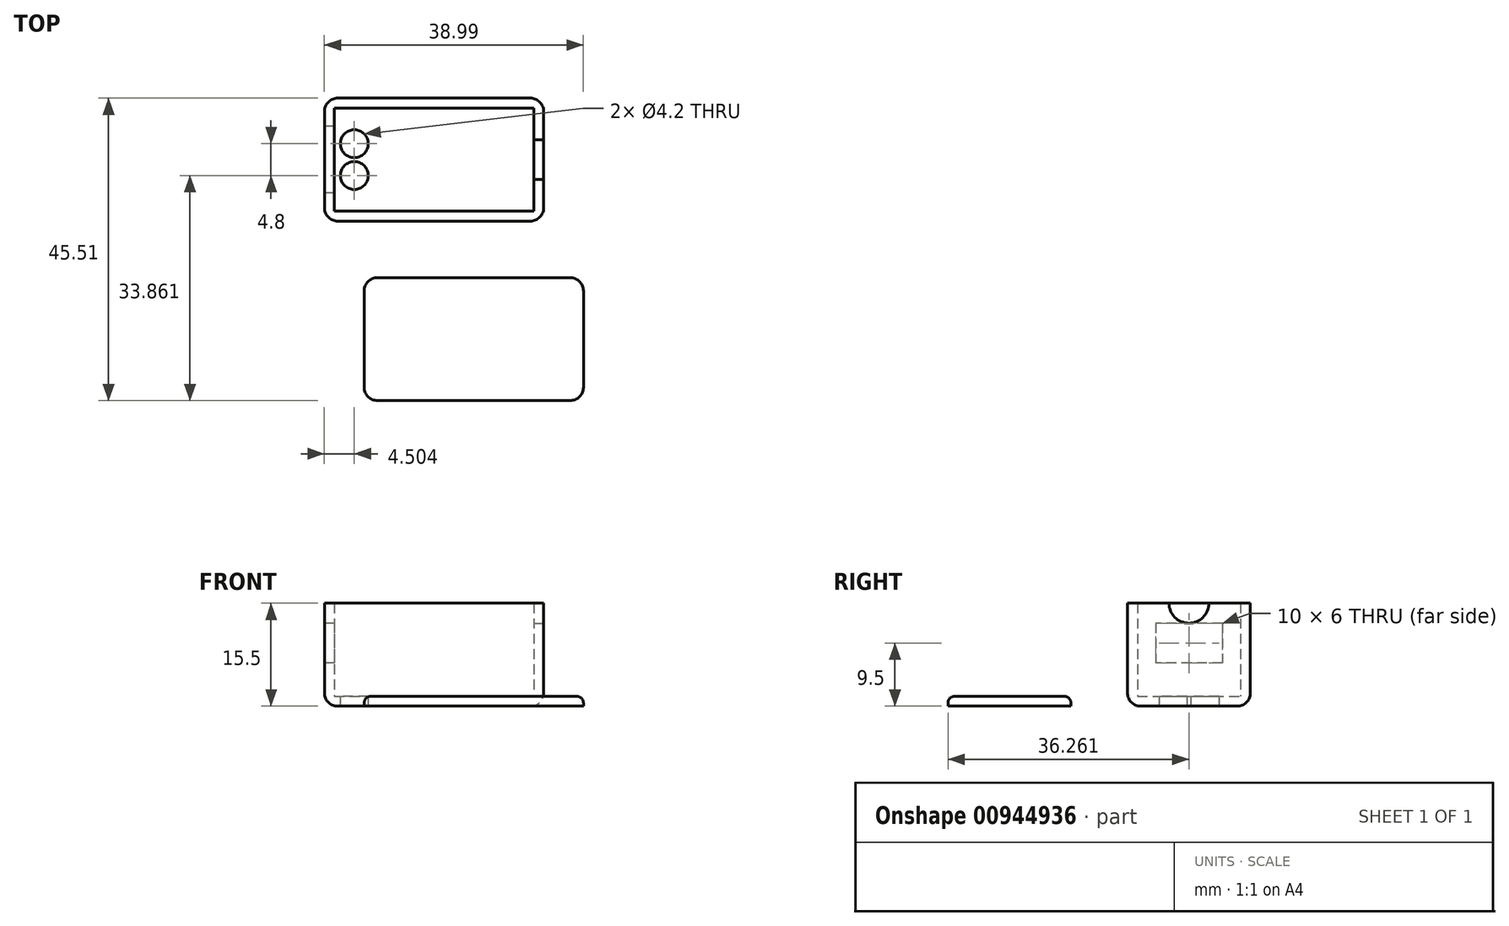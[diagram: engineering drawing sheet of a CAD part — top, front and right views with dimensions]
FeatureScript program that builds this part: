
annotation { "Feature Type Name" : "Feature", "Feature Type Description" : "" }
export const myFeature = defineFeature(function(context is Context, id is Id, definition is map)
    precondition{}
    {
        {
            var Q0;
            Q0=qCreatedBy(makeId("Top.planeOp"),FACE);
            var sketch = newSketch(context, id + "F0", { "sketchPlane" : qUnion([Q0])});
            skLineSegment(sketch, "E0.bottom", {"start": v(-24.86, -16.36) * mm, "end": v(5.14, -16.36) * mm});
            skLineSegment(sketch, "E0.top", {"start": v(-24.86, -0.86) * mm, "end": v(5.14, -0.86) * mm});
            skLineSegment(sketch, "E0.left", {"start": v(-24.86, -16.36) * mm, "end": v(-24.86, -0.86) * mm});
            skLineSegment(sketch, "E0.right", {"start": v(5.14, -16.36) * mm, "end": v(5.14, -0.86) * mm});
            skLineSegment(sketch, "E1.0", {"start": v(-26.36, -15.86) * mm, "end": v(-26.36, -1.36) * mm});
            skLineSegment(sketch, "E1.1", {"start": v(-24.36, -17.86) * mm, "end": v(4.64, -17.86) * mm});
            skLineSegment(sketch, "E1.2", {"start": v(6.64, -15.86) * mm, "end": v(6.64, -1.36) * mm});
            skLineSegment(sketch, "E1.3", {"start": v(-24.36, 0.64) * mm, "end": v(4.64, 0.64) * mm});
            skPoint(sketch, "E2.visualSharp", {"position": v(6.64, 0.64) * mm});
            skArc(sketch, "E2.filletArc", {"start": v(6.64, -1.36) * mm, "mid": v(6.06, 0.06) * mm, "end": v(4.64, 0.64) * mm});
            skPoint(sketch, "E3.visualSharp", {"position": v(6.64, -17.86) * mm});
            skArc(sketch, "E3.filletArc", {"start": v(4.64, -17.86) * mm, "mid": v(6.06, -17.27) * mm, "end": v(6.64, -15.86) * mm});
            skPoint(sketch, "E4.visualSharp", {"position": v(-26.36, -17.86) * mm});
            skArc(sketch, "E4.filletArc", {"start": v(-26.36, -15.86) * mm, "mid": v(-25.77, -17.27) * mm, "end": v(-24.36, -17.86) * mm});
            skPoint(sketch, "E5.visualSharp", {"position": v(-26.36, 0.64) * mm});
            skArc(sketch, "E5.filletArc", {"start": v(-24.36, 0.64) * mm, "mid": v(-25.77, 0.06) * mm, "end": v(-26.36, -1.36) * mm});
            skLineSegment(sketch, "E6", {"start": v(-24.86, -8.6) * mm, "end": v(-21.86, -8.6) * mm, "construction": true});
            skLineSegment(sketch, "E7", {"start": v(-21.86, -8.6) * mm, "end": v(-21.86, -6.2) * mm, "construction": true});
            skLineSegment(sketch, "E8", {"start": v(-21.86, -8.6) * mm, "end": v(-21.86, -11) * mm, "construction": true});
            skCircle(sketch, "E9", {"center": v(-21.86, -6.2) * mm, "radius": 2.1 * mm});
            skCircle(sketch, "E10", {"center": v(-21.86, -11) * mm, "radius": 2.1 * mm});
            skSolve(sketch);
        }
        {
            var Q0;
            Q0=makeQuery(id+"F0.imprint","IMPRINT",FACE,{"disambiguationData":[TD([[makeQuery(id+"F0.imprint","IMPRINT",EDGE,{"derivedFrom":sQuery(id+"F0.wireOp",EDGE,"E0.bottom")}),-1.0]])]});
            extrude(context, id + "F1", {"entities" : qUnion([Q0]), "depth" : 15.5 * mm, "offsetDistance" : 25 * mm});
        }
        {
            var Q0;
            Q0=makeQuery(id+"F0.imprint","IMPRINT",FACE,{"disambiguationData":[TD([[makeQuery(id+"F0.imprint","IMPRINT",EDGE,{"derivedFrom":sQuery(id+"F0.wireOp",EDGE,"E0.bottom")}),1.0]])]});
            extrude(context, id + "F2", {"entities" : qUnion([Q0]), "operationType" : NewBodyOperationType.ADD, "depth" : 1.5 * mm, "offsetDistance" : 25 * mm});
        }
        {
            var Q0;
            Q0=makeQuery(id+"F1.opExtrude","SWEPT_FACE",FACE,{"disambiguationData":[OSD([sQuery(id+"F0.wireOp",EDGE,"E1.0")])]});
            var sketch = newSketch(context, id + "F3", { "sketchPlane" : qUnion([Q0])});
            skLineSegment(sketch, "E11", {"start": v(8.6, 15.5) * mm, "end": v(8.6, 12.5) * mm, "construction": true});
            skLineSegment(sketch, "E12", {"start": v(8.6, 12.5) * mm, "end": v(3.6, 12.5) * mm, "construction": true});
            skLineSegment(sketch, "E13.bottom", {"start": v(3.6, 12.5) * mm, "end": v(13.6, 12.5) * mm});
            skLineSegment(sketch, "E13.top", {"start": v(3.6, 6.5) * mm, "end": v(13.6, 6.5) * mm});
            skLineSegment(sketch, "E13.left", {"start": v(3.6, 12.5) * mm, "end": v(3.6, 6.5) * mm});
            skLineSegment(sketch, "E13.right", {"start": v(13.6, 12.5) * mm, "end": v(13.6, 6.5) * mm});
            skSolve(sketch);
        }
        {
            var Q0;
            Q0=makeQuery(id+"F3.imprint","IMPRINT",FACE,{"disambiguationData":[TD([[makeQuery(id+"F3.imprint","IMPRINT",EDGE,{"derivedFrom":sQuery(id+"F3.wireOp",EDGE,"E13.bottom")}),-1.0]])]});
            extrude(context, id + "F4", {"entities" : qUnion([Q0]), "operationType" : NewBodyOperationType.REMOVE, "oppositeDirection" : true, "depth" : 2 * mm, "offsetDistance" : 25 * mm});
        }
        {
            var Q0;
            Q0=qCreatedBy(makeId("Top.planeOp"),FACE);
            var sketch = newSketch(context, id + "F5", { "sketchPlane" : qUnion([Q0])});
            skLineSegment(sketch, "E14.bottom", {"start": v(-18.37, -26.37) * mm, "end": v(10.63, -26.37) * mm});
            skLineSegment(sketch, "E14.top", {"start": v(-18.37, -44.87) * mm, "end": v(10.63, -44.87) * mm});
            skLineSegment(sketch, "E14.left", {"start": v(-20.37, -28.37) * mm, "end": v(-20.37, -42.87) * mm});
            skLineSegment(sketch, "E14.right", {"start": v(12.63, -28.37) * mm, "end": v(12.63, -42.87) * mm});
            skPoint(sketch, "E15.visualSharp", {"position": v(12.63, -26.37) * mm});
            skArc(sketch, "E15.filletArc", {"start": v(12.63, -28.37) * mm, "mid": v(12.05, -26.96) * mm, "end": v(10.63, -26.37) * mm});
            skPoint(sketch, "E16.visualSharp", {"position": v(12.63, -44.87) * mm});
            skArc(sketch, "E16.filletArc", {"start": v(10.63, -44.87) * mm, "mid": v(12.05, -44.29) * mm, "end": v(12.63, -42.87) * mm});
            skPoint(sketch, "E17.visualSharp", {"position": v(-20.37, -44.87) * mm});
            skArc(sketch, "E17.filletArc", {"start": v(-20.37, -42.87) * mm, "mid": v(-19.78, -44.29) * mm, "end": v(-18.37, -44.87) * mm});
            skPoint(sketch, "E18.visualSharp", {"position": v(-20.37, -26.37) * mm});
            skArc(sketch, "E18.filletArc", {"start": v(-18.37, -26.37) * mm, "mid": v(-19.78, -26.96) * mm, "end": v(-20.37, -28.37) * mm});
            skSolve(sketch);
        }
        {
            var Q0;
            Q0=makeQuery(id+"F5.imprint","IMPRINT",FACE,{"disambiguationData":[TD([[makeQuery(id+"F5.imprint","IMPRINT",EDGE,{"derivedFrom":sQuery(id+"F5.wireOp",EDGE,"E14.bottom")}),-1.0]])]});
            extrude(context, id + "F6", {"entities" : qUnion([Q0]), "depth" : 1.5 * mm, "offsetDistance" : 25 * mm});
        }
        {
            var Q0;
            Q0=makeQuery(id+"F6.opExtrude","CAP_EDGE",EDGE,{"disambiguationData":[OSD([sQuery(id+"F5.wireOp",EDGE,"E14.top")])],"isStart":false});
            fillet(context, id + "F7", {"entities" : qUnion([Q0]), "radius" : 1 * mm, "tangentPropagation" : true, "allowEdgeOverflow" : false});
        }
        {
            var Q0;
            Q0=makeQuery(id+"F1.opExtrude","CAP_EDGE",EDGE,{"disambiguationData":[OSD([sQuery(id+"F0.wireOp",EDGE,"E1.0")])],"isStart":true});
            var Q1;
            Q1=makeQuery(id+"F1.opExtrude","CAP_EDGE",EDGE,{"disambiguationData":[OSD([sQuery(id+"F0.wireOp",EDGE,"E1.3")])],"isStart":true});
            var Q2;
            Q2=makeQuery(id+"F1.opExtrude","CAP_EDGE",EDGE,{"disambiguationData":[OSD([sQuery(id+"F0.wireOp",EDGE,"E1.2")])],"isStart":true});
            var Q3;
            Q3=makeQuery(id+"F1.opExtrude","CAP_EDGE",EDGE,{"disambiguationData":[OSD([sQuery(id+"F0.wireOp",EDGE,"E1.1")])],"isStart":true});
            var Q4;
            Q4=makeQuery(id+"F1.opExtrude","CAP_EDGE",EDGE,{"disambiguationData":[OSD([sQuery(id+"F0.wireOp",EDGE,"E3.filletArc")])],"isStart":true});
            var Q5;
            Q5=makeQuery(id+"F1.opExtrude","CAP_EDGE",EDGE,{"disambiguationData":[OSD([sQuery(id+"F0.wireOp",EDGE,"E2.filletArc")])],"isStart":true});
            var Q6;
            Q6=makeQuery(id+"F1.opExtrude","CAP_EDGE",EDGE,{"disambiguationData":[OSD([sQuery(id+"F0.wireOp",EDGE,"E5.filletArc")])],"isStart":true});
            var Q7;
            Q7=makeQuery(id+"F1.opExtrude","CAP_EDGE",EDGE,{"disambiguationData":[OSD([sQuery(id+"F0.wireOp",EDGE,"E4.filletArc")])],"isStart":true});
            fillet(context, id + "F8", {"entities" : qUnion([Q0, Q1, Q2, Q3, Q4, Q5, Q6, Q7]), "radius" : 2 * mm, "allowEdgeOverflow" : false});
        }
        {
            var Q0;
            Q0=makeQuery(id+"F1.opExtrude","SWEPT_FACE",FACE,{"disambiguationData":[OSD([sQuery(id+"F0.wireOp",EDGE,"E1.2")])]});
            var sketch = newSketch(context, id + "F9", { "sketchPlane" : qUnion([Q0])});
            skCircle(sketch, "E19", {"center": v(-8.6, 15.5) * mm, "radius": 3 * mm});
            skSolve(sketch);
        }
        {
            var Q0;
            {var subQ0=sQuery(id+"F9.wireOp",EDGE,"E19");var subQ1=makeQuery(id+"F1.opExtrude","CAP_EDGE",EDGE,{"disambiguationData":[OSD([sQuery(id+"F0.wireOp",EDGE,"E1.2")])],"isStart":false});var subQ2=makeQuery(id+"F9.imprint","INTERSECT",VERTEX,{"disambiguationData":[OD(0.0)],"derivedFrom":[subQ1,subQ0]});Q0=makeQuery(id+"F9.imprint","IMPRINT",FACE,{"disambiguationData":[TD([[makeQuery(id+"F9.imprint","IMPRINT",EDGE,{"disambiguationData":[TD([[subQ2,-1.0]])],"derivedFrom":subQ0}),1.0]])]});}
            extrude(context, id + "F10", {"entities" : qUnion([Q0]), "operationType" : NewBodyOperationType.REMOVE, "oppositeDirection" : true, "depth" : 2 * mm, "offsetDistance" : 25 * mm});
        }
    });
